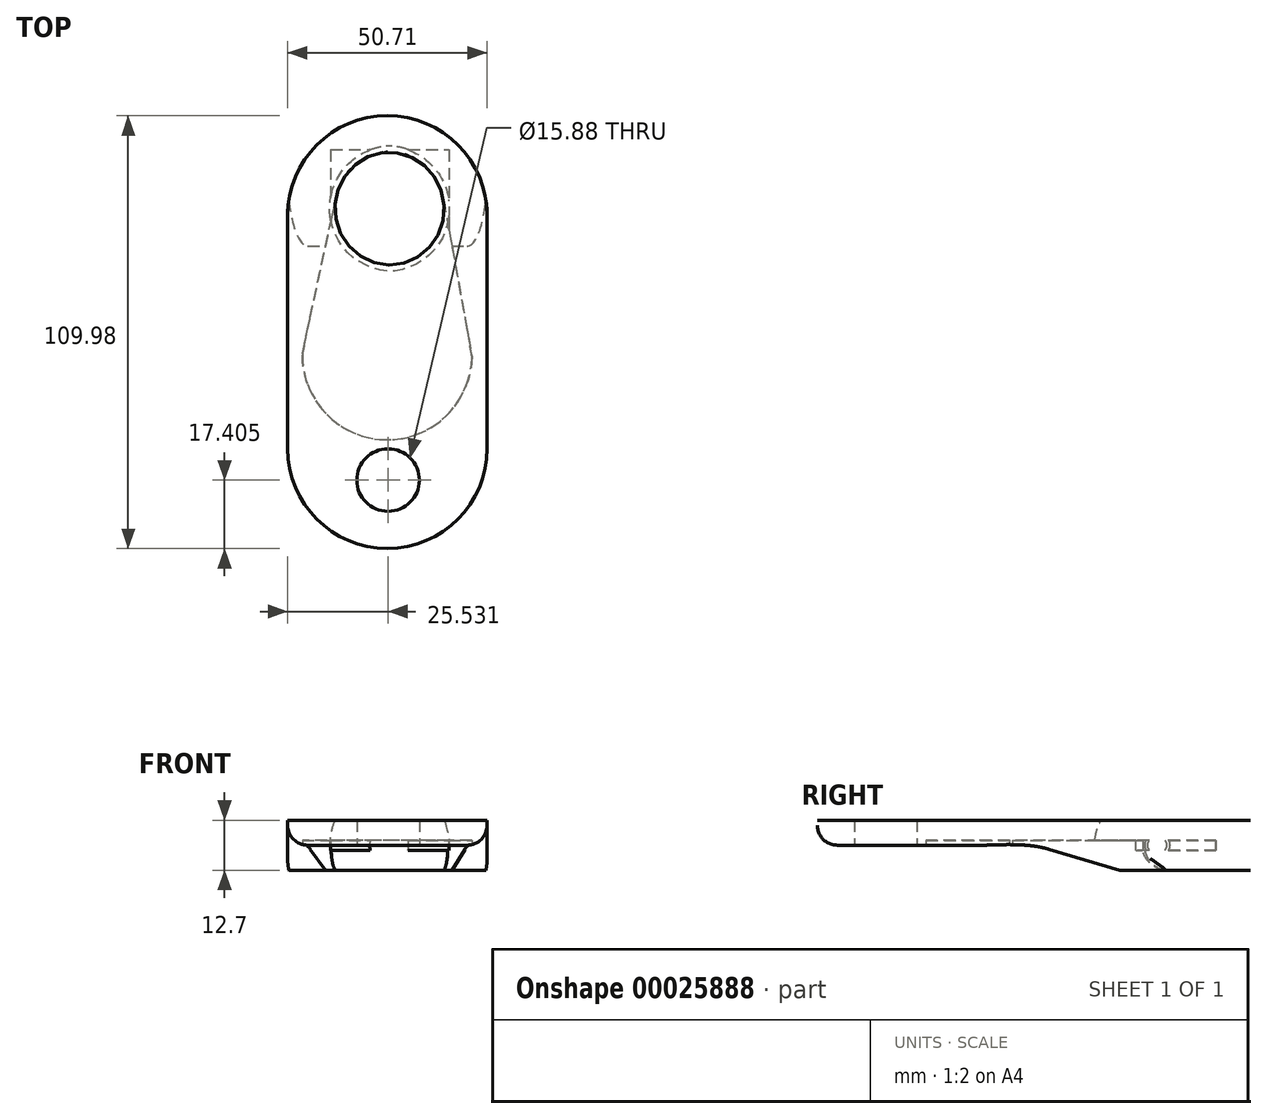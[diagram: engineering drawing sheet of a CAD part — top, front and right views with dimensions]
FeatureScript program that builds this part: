
annotation { "Feature Type Name" : "Feature", "Feature Type Description" : "" }
export const myFeature = defineFeature(function(context is Context, id is Id, definition is map)
    precondition{}
    {
        {
            var Q0;
            Q0=qCreatedBy(makeId("Top.planeOp"),FACE);
            var sketch = newSketch(context, id + "F0", { "sketchPlane" : qUnion([Q0])});
            skLineSegment(sketch, "E0.bottom", {"start": v(-12.1, 58.43) * mm, "end": v(17.92, 58.43) * mm});
            skLineSegment(sketch, "E0.top", {"start": v(-12.1, 28.4) * mm, "end": v(17.92, 28.4) * mm});
            skLineSegment(sketch, "E0.left", {"start": v(-12.1, 58.43) * mm, "end": v(-12.1, 28.4) * mm});
            skLineSegment(sketch, "E0.right", {"start": v(17.92, 58.43) * mm, "end": v(17.92, 28.4) * mm});
            skSolve(sketch);
        }
        {
            var Q0;
            Q0=qCreatedBy(makeId("Top.planeOp"),FACE);
            var sketch = newSketch(context, id + "F1", { "sketchPlane" : qUnion([Q0])});
            skArc(sketch, "E1", {"start": v(3.76, 27.52) * mm, "mid": v(18.06, 44.36) * mm, "end": v(1.92, 59.44) * mm});
            skLineSegment(sketch, "E2", {"start": v(3.76, 27.52) * mm, "end": v(1.92, 59.44) * mm});
            skSolve(sketch);
        }
        {
            var Q0;
            Q0=makeQuery(id+"F1.imprint","IMPRINT",FACE,{"disambiguationData":[TD([[makeQuery(id+"F1.imprint","IMPRINT",EDGE,{"derivedFrom":sQuery(id+"F1.wireOp",EDGE,"E1")}),1.0]])]});
            var Q1;
            Q1=sQuery(id+"F1.wireOp",EDGE,"E1");
            var Q2;
            Q2=sQuery(id+"F1.wireOp",EDGE,"E2");
            revolve(context, id + "F2", {"entities" : qUnion([Q0]), "surfaceEntities" : qUnion([Q1]), "axis" : qUnion([Q2]), "revolveType" : RevolveType.FULL});
        }
        {
            var Q0;
            Q0=makeQuery(id+"F0.imprint","IMPRINT",FACE,{"disambiguationData":[TD([[makeQuery(id+"F0.imprint","IMPRINT",EDGE,{"derivedFrom":sQuery(id+"F0.wireOp",EDGE,"E0.bottom")}),-1.0]])]});
            extrude(context, id + "F3", {"entities" : qUnion([Q0]), "depth" : 1.27 * mm, "hasSecondDirection" : true, "secondDirectionOppositeDirection" : true, "secondDirectionDepth" : 1.27 * mm});
        }
        {
            var Q0;
            Q0=qCreatedBy(makeId("Top.planeOp"),FACE);
            var sketch = newSketch(context, id + "F4", { "sketchPlane" : qUnion([Q0])});
            skLineSegment(sketch, "E3.bottom", {"start": v(-23.08, 67.1) * mm, "end": v(27.63, 67.1) * mm});
            skLineSegment(sketch, "E3.top", {"start": v(-23.08, -42.89) * mm, "end": v(27.63, -42.89) * mm});
            skLineSegment(sketch, "E3.left", {"start": v(-23.08, 67.1) * mm, "end": v(-23.08, -42.89) * mm});
            skLineSegment(sketch, "E3.right", {"start": v(27.63, 67.1) * mm, "end": v(27.63, -42.89) * mm});
            skSolve(sketch);
        }
        {
            var Q0;
            Q0=makeQuery(id+"F4.imprint","IMPRINT",FACE,{"disambiguationData":[TD([[makeQuery(id+"F4.imprint","IMPRINT",EDGE,{"derivedFrom":sQuery(id+"F4.wireOp",EDGE,"E3.bottom")}),-1.0]])]});
            extrude(context, id + "F5", {"entities" : qUnion([Q0]), "depth" : 6.35 * mm, "hasSecondDirection" : true, "secondDirectionOppositeDirection" : true, "secondDirectionDepth" : 6.35 * mm});
        }
        {
            var Q0;
            Q0=makeQuery(id+"F2.opRevolve","SWEPT_BODY",BODY,{"disambiguationData":[OSD([sQuery(id+"F1.wireOp",EDGE,"E1"),sQuery(id+"F1.wireOp",EDGE,"E2")])]});
            var Q1;
            Q1=makeQuery(id+"F3.opExtrude","SWEPT_BODY",BODY,{"disambiguationData":[OSD([sQuery(id+"F0.wireOp",EDGE,"E0.bottom"),sQuery(id+"F0.wireOp",EDGE,"E0.top"),sQuery(id+"F0.wireOp",EDGE,"E0.left"),sQuery(id+"F0.wireOp",EDGE,"E0.right")])]});
            booleanBodies(context, id + "F6", {"operationType" : BooleanOperationType.UNION, "tools" : qUnion([Q0, Q1])});
        }
        {
            var Q0;
            Q0=makeQuery(id+"F2.opRevolve","SWEPT_BODY",BODY,{"disambiguationData":[OSD([sQuery(id+"F1.wireOp",EDGE,"E1"),sQuery(id+"F1.wireOp",EDGE,"E2")])]});
            var Q1;
            Q1=makeQuery(id+"F5.opExtrude","SWEPT_BODY",BODY,{"disambiguationData":[OSD([sQuery(id+"F4.wireOp",EDGE,"E3.bottom"),sQuery(id+"F4.wireOp",EDGE,"E3.top"),sQuery(id+"F4.wireOp",EDGE,"E3.left"),sQuery(id+"F4.wireOp",EDGE,"E3.right")])]});
            booleanBodies(context, id + "F7", {"operationType" : BooleanOperationType.SUBTRACTION, "tools" : qUnion([Q0]), "targets" : qUnion([Q1])});
        }
        {
            var Q0;
            Q0=makeQuery(id+"F5.opExtrude","CAP_FACE",FACE,{"disambiguationData":[OSD([sQuery(id+"F4.wireOp",EDGE,"E3.bottom"),sQuery(id+"F4.wireOp",EDGE,"E3.top"),sQuery(id+"F4.wireOp",EDGE,"E3.left"),sQuery(id+"F4.wireOp",EDGE,"E3.right")])],"isStart":true});
            var sketch = newSketch(context, id + "F8", { "sketchPlane" : qUnion([Q0])});
            skArc(sketch, "E4", {"start": v(23.75, -5.94) * mm, "mid": v(1.86, 15.23) * mm, "end": v(-19.31, -6.66) * mm});
            skLineSegment(sketch, "E5", {"start": v(-19.31, -6.66) * mm, "end": v(-10.88, -45.61) * mm});
            skLineSegment(sketch, "E6", {"start": v(-10.88, -45.61) * mm, "end": v(16.54, -45.61) * mm});
            skLineSegment(sketch, "E7", {"start": v(16.54, -45.61) * mm, "end": v(23.75, -5.94) * mm});
            skSolve(sketch);
        }
        {
            var Q0;
            {var subQ4=sQuery(id+"F8.wireOp",EDGE,"E4");Q0=makeQuery(id+"F8.imprint","IMPRINT",FACE,{"disambiguationData":[TD([[makeQuery(id+"F8.imprint","IMPRINT",EDGE,{"derivedFrom":subQ4}),1.0]])]});}
            extrude(context, id + "F9", {"entities" : qUnion([Q0]), "operationType" : NewBodyOperationType.REMOVE, "oppositeDirection" : true, "depth" : 7.62 * mm});
        }
        {
            var Q0;
            Q0=makeQuery(id+"F5.opExtrude","SWEPT_FACE",FACE,{"disambiguationData":[OSD([sQuery(id+"F4.wireOp",EDGE,"E3.right")])]});
            var sketch = newSketch(context, id + "F10", { "sketchPlane" : qUnion([Q0])});
            skLineSegment(sketch, "E8", {"start": v(34.01, -6.35) * mm, "end": v(12.4, 0) * mm});
            skLineSegment(sketch, "E9", {"start": v(12.4, 0) * mm, "end": v(-42.89, 0) * mm});
            skLineSegment(sketch, "E10", {"start": v(-42.89, 0) * mm, "end": v(-42.89, -6.35) * mm});
            skLineSegment(sketch, "E11", {"start": v(-42.89, -6.35) * mm, "end": v(34.01, -6.35) * mm});
            skSolve(sketch);
        }
        {
            var Q0;
            Q0=makeQuery(id+"F10.imprint","IMPRINT",FACE,{"disambiguationData":[TD([[makeQuery(id+"F10.imprint","IMPRINT",EDGE,{"derivedFrom":sQuery(id+"F10.wireOp",EDGE,"E8")}),1.0]])]});
            extrude(context, id + "F11", {"entities" : qUnion([Q0]), "operationType" : NewBodyOperationType.REMOVE, "endBound" : BoundingType.THROUGH_ALL, "oppositeDirection" : true, "depth" : 25.4 * mm});
        }
        {
            var Q0;
            Q0=makeQuery(id+"F11.boolean.opBoolean","COPY",FACE,{"derivedFrom":makeQuery(id+"F11.opExtrude","SWEPT_FACE",FACE,{"disambiguationData":[OSD([sQuery(id+"F10.wireOp",EDGE,"E9")])]})});
            var sketch = newSketch(context, id + "F12", { "sketchPlane" : qUnion([Q0])});
            skCircle(sketch, "E12", {"center": v(2.45, 25.49) * mm, "radius": 7.94 * mm});
            skSolve(sketch);
        }
        {
            var Q0;
            Q0=makeQuery(id+"F12.imprint","IMPRINT",FACE,{"disambiguationData":[TD([[makeQuery(id+"F12.imprint","IMPRINT",EDGE,{"derivedFrom":sQuery(id+"F12.wireOp",EDGE,"E12")}),1.0]])]});
            extrude(context, id + "F13", {"entities" : qUnion([Q0]), "operationType" : NewBodyOperationType.REMOVE, "endBound" : BoundingType.THROUGH_ALL, "oppositeDirection" : true, "depth" : 25.4 * mm});
        }
        {
            var Q0;
            Q0=makeQuery(id+"F5.opExtrude","SWEPT_EDGE",EDGE,{"disambiguationData":[OSD([sQuery(id+"F4.wireOp",EDGE,"E3.top"),sQuery(id+"F4.wireOp",EDGE,"E3.right")])]});
            var Q1;
            Q1=makeQuery(id+"F5.opExtrude","SWEPT_EDGE",EDGE,{"disambiguationData":[OSD([sQuery(id+"F4.wireOp",EDGE,"E3.top"),sQuery(id+"F4.wireOp",EDGE,"E3.left")])]});
            var Q2;
            Q2=makeQuery(id+"F5.opExtrude","SWEPT_EDGE",EDGE,{"disambiguationData":[OSD([sQuery(id+"F4.wireOp",EDGE,"E3.bottom"),sQuery(id+"F4.wireOp",EDGE,"E3.right")])]});
            var Q3;
            Q3=makeQuery(id+"F5.opExtrude","SWEPT_EDGE",EDGE,{"disambiguationData":[OSD([sQuery(id+"F4.wireOp",EDGE,"E3.bottom"),sQuery(id+"F4.wireOp",EDGE,"E3.left")])]});
            fillet(context, id + "F14", {"entities" : qUnion([Q0, Q1, Q2, Q3]), "radius" : 25.4 * mm, "tangentPropagation" : true, "allowEdgeOverflow" : false});
        }
        {
            var Q0;
            Q0=makeQuery(id+"F11.boolean.opBoolean","COPY",EDGE,{"disambiguationData":[OD(1.0)],"derivedFrom":makeQuery(id+"F11.opExtrude","SWEPT_EDGE",EDGE,{"disambiguationData":[OSD([sQuery(id+"F4.wireOp",EDGE,"E3.right"),sQuery(id+"F10.wireOp",EDGE,"E8"),sQuery(id+"F10.wireOp",EDGE,"E11")])]})});
            var Q1;
            Q1=makeQuery(id+"F11.boolean.opBoolean","COPY",EDGE,{"disambiguationData":[OD(0.0)],"derivedFrom":makeQuery(id+"F11.opExtrude","SWEPT_EDGE",EDGE,{"disambiguationData":[OSD([sQuery(id+"F4.wireOp",EDGE,"E3.right"),sQuery(id+"F10.wireOp",EDGE,"E8"),sQuery(id+"F10.wireOp",EDGE,"E11")])]})});
            var Q2;
            Q2=makeQuery(id+"F11.boolean.opBoolean","COPY",EDGE,{"disambiguationData":[OD(0.0)],"derivedFrom":makeQuery(id+"F11.opExtrude","SWEPT_EDGE",EDGE,{"disambiguationData":[OSD([sQuery(id+"F10.wireOp",EDGE,"E8"),sQuery(id+"F10.wireOp",EDGE,"E9")])]})});
            var Q3;
            Q3=makeQuery(id+"F11.boolean.opBoolean","COPY",EDGE,{"disambiguationData":[OD(1.0)],"derivedFrom":makeQuery(id+"F11.opExtrude","SWEPT_EDGE",EDGE,{"disambiguationData":[OSD([sQuery(id+"F10.wireOp",EDGE,"E8"),sQuery(id+"F10.wireOp",EDGE,"E9")])]})});
            fillet(context, id + "F15", {"entities" : qUnion([Q0, Q1, Q2, Q3]), "radius" : 25.4 * mm, "tangentPropagation" : true, "allowEdgeOverflow" : false});
        }
        {
            var Q0;
            Q0=makeQuery(id+"F11.boolean.opBoolean","COPY",EDGE,{"derivedFrom":makeQuery(id+"F11.opExtrude","CAP_EDGE",EDGE,{"disambiguationData":[OSD([sQuery(id+"F10.wireOp",EDGE,"E9")])],"isStart":true})});
            var Q1;
            Q1=makeQuery(id+"F14.opFillet","BLEND_EDGE",EDGE,{"blendedFrom":[makeQuery(id+"F5.opExtrude","SWEPT_EDGE",EDGE,{"disambiguationData":[OSD([sQuery(id+"F4.wireOp",EDGE,"E3.top"),sQuery(id+"F4.wireOp",EDGE,"E3.right")])]}),makeQuery(id+"F11.boolean.opBoolean","COPY",FACE,{"derivedFrom":makeQuery(id+"F11.opExtrude","SWEPT_FACE",FACE,{"disambiguationData":[OSD([sQuery(id+"F10.wireOp",EDGE,"E9")])]})})],"blendedInto":[makeQuery(id+"F11.boolean.opBoolean","COPY",FACE,{"derivedFrom":makeQuery(id+"F11.opExtrude","SWEPT_FACE",FACE,{"disambiguationData":[OSD([sQuery(id+"F10.wireOp",EDGE,"E9")])]})})]});
            var Q2;
            Q2=makeQuery(id+"F14.opFillet","BLEND_EDGE",EDGE,{"blendedFrom":[makeQuery(id+"F5.opExtrude","SWEPT_EDGE",EDGE,{"disambiguationData":[OSD([sQuery(id+"F4.wireOp",EDGE,"E3.top"),sQuery(id+"F4.wireOp",EDGE,"E3.left")])]}),makeQuery(id+"F11.boolean.opBoolean","COPY",FACE,{"derivedFrom":makeQuery(id+"F11.opExtrude","SWEPT_FACE",FACE,{"disambiguationData":[OSD([sQuery(id+"F10.wireOp",EDGE,"E9")])]})})],"blendedInto":[makeQuery(id+"F11.boolean.opBoolean","COPY",FACE,{"derivedFrom":makeQuery(id+"F11.opExtrude","SWEPT_FACE",FACE,{"disambiguationData":[OSD([sQuery(id+"F10.wireOp",EDGE,"E9")])]})})]});
            fillet(context, id + "F16", {"entities" : qUnion([Q0, Q1, Q2]), "radius" : 5.08 * mm, "tangentPropagation" : true, "allowEdgeOverflow" : false});
        }
    });
